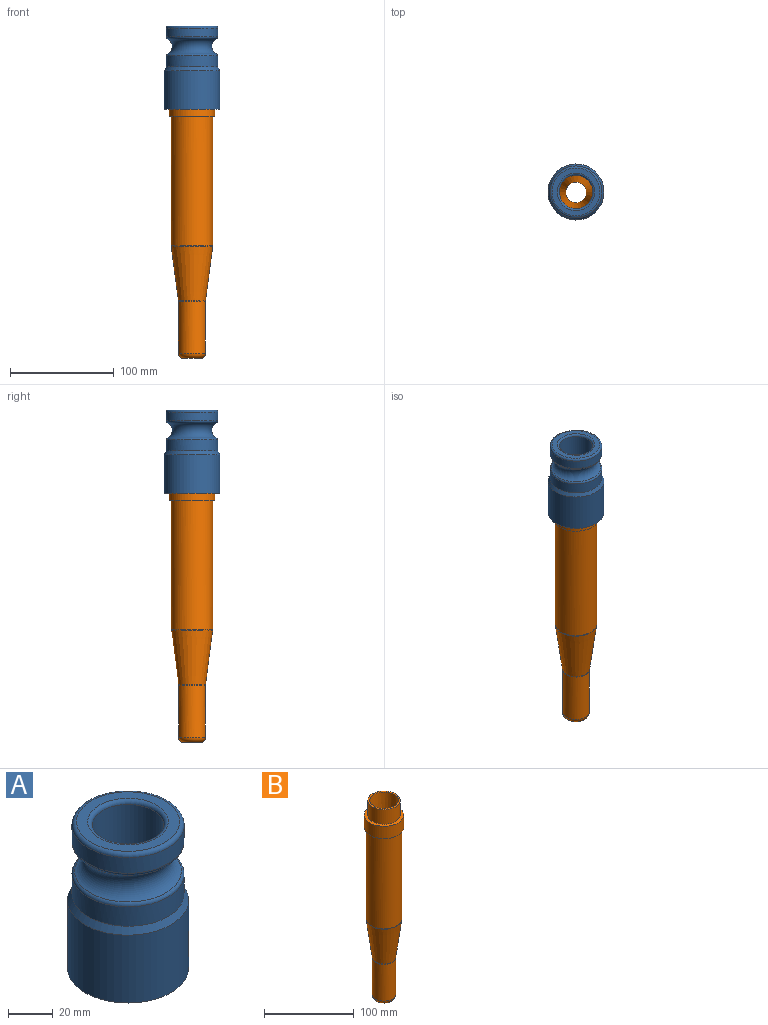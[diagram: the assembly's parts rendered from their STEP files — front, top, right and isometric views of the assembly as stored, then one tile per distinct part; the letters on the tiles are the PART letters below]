
ASSEMBLY  parts=2 mates=1
PART A: 14 faces, bbox 58.4x58.4x80 mm
  f0: cylinder r=16mm len=48mm, axis (0,0,1), area 4825.5mm2, adj f8,f13
  f1: plane 46x46mm, normal (0,0,1), area 644mm2, adj f8,f9
  f2: cylinder r=25mm len=50mm, axis (0,0,1), area 1347.9mm2, adj f9,f10
  f3: torus R=27mm, axis (0,0,1), area 2409.6mm2, adj f10,f11
  f4: cylinder r=25mm len=50mm, axis (0,0,1), area 1662mm2, adj f5,f11
  f5: cone r=25mm half-angle=30deg, axis (0,0,-1), area 653.5mm2, adj f4,f6
  f6: cylinder r=27mm len=54mm, axis (0,0,1), area 6284.4mm2, adj f5,f7
  f7: plane 54x54mm, normal (0,0,-1), area 1272.3mm2, adj f6,f12
  f8: torus R=18mm, axis (0,0,1), area 330.2mm2, adj f0,f1
  f9: torus R=23mm, axis (0,0,1), area 479.1mm2, adj f1,f2
  f10: torus R=23mm, axis (0,0,-1), area 358.1mm2, adj f2,f3
  f11: torus R=23mm, axis (0,0,-1), area 358.1mm2, adj f3,f4
  f12: cylinder r=18mm len=36mm, axis (0,0,-1), area 3392.9mm2, adj f7,f13
  f13: plane 36x36mm, normal (0,0,-1), area 213.6mm2, adj f0,f12
PART B: 13 faces, bbox 44x44x270.4 mm
  f0: cylinder r=22mm len=44mm, axis (0,0,1), area 2337.6mm2, adj f1,f9
  f1: plane 44x44mm, normal (0,0,-1), area 263.9mm2, adj f0,f2
  f2: cylinder r=20mm len=124.67mm, axis (0,0,1), area 15666.7mm2, adj f1,f11
  f3: cone r=20mm half-angle=7.5deg, axis (0,0,1), area 5483.5mm2, adj f11,f12
  f4: cylinder r=13mm len=50.09mm, axis (0,0,1), area 4091.4mm2, adj f10,f12
  f5: cylinder r=10mm len=55mm, axis (0,0,1), area 3455.8mm2, adj f6,f10
  f6: cone r=10mm half-angle=1.6deg, axis (0,0,1), area 17568.3mm2, adj f5,f7
  f7: plane 36x36mm, normal (0,0,1), area 213.6mm2, adj f6,f8
  f8: cylinder r=18mm len=36mm, axis (0,0,1), area 2261.9mm2, adj f7,f9
  f9: plane 44x44mm, normal (0,0,1), area 502.7mm2, adj f0,f8
  f10: torus R=8mm, axis (0,0,-1), area 435.3mm2, adj f4,f5
  f11: torus R=15mm, axis (0,0,-1), area 82.3mm2, adj f2,f3
  f12: torus R=18mm, axis (0,0,1), area 53.6mm2, adj f3,f4
PLACE A t=(-0.74,-0.36,73.67)mm
PLACE B t=(-0.74,-0.36,-2.86)mm
MATE fastened A.f12 <-> B.f0  axis (0,0,-1) through (-0.74,-0.36,66.63)mm
